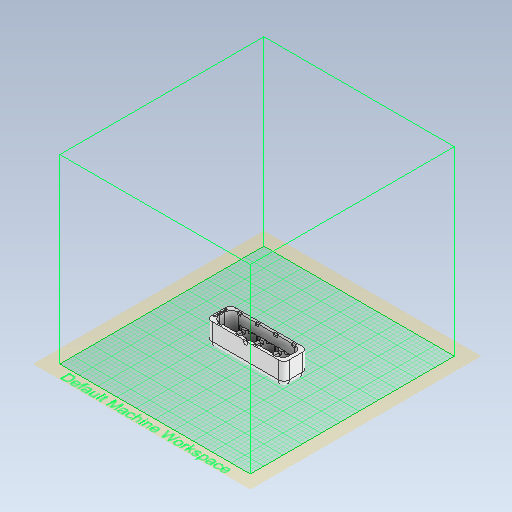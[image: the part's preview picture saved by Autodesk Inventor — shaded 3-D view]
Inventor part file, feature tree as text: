
AUTODESK INVENTOR PART (.ipt)
format: ipt  version: 2021 (Build 250183000, 183)  size: 2,136,576 bytes
history: native  units: in
note: dims shown in document units (in); Inventor stores cm internally (conversion verified against a paired STEP export)
features: extrude x8, other x7, fillet x2
ambient origin geometry x8: Origin, YZ Plane, XZ Plane, XY Plane, X Axis, Y Axis, Z Axis, Center Point
bodies: Body1 (feature_tree)
feature tree (17):
  extrude  "Base"  Depth=4.8819in
  other  "Top Indent Sketch"
  extrude  "Top"  Depth=2.0472in
  extrude  "Walls"  Depth=1.5748in TaperAngle=0.0deg
  fillet  "Outer"  Radius=0.7874in
  extrude  "Outer Wire"  Depth=0.7874in
  extrude  "Wall Holes"  Depth=0.7874in
  extrude  "Text"  Depth=0.7874in
  extrude  "Inner Sketch"  Depth=1.0236in
  fillet  "Inner Fillet"  Radius=1.0236in
  extrude  "Top Indent"  Depth=1.0236in
  other  "Base Sketch"
  other  "Walls Sketch"
  other  "Outer Wire Sketch"
  other  "Wall Holes Sketch"
  other  "Text Sketch"
  other  "Inner Support Sketch"
